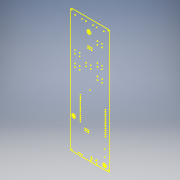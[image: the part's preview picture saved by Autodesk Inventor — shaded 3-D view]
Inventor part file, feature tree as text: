
AUTODESK INVENTOR PART (.ipt)
format: ipt  version: 2019 (Build 230136000, 136)  size: 111,616 bytes
history: native  units: mm
features: other x3, sketch x1, reference x1
ambient origin geometry x8: Origin, YZ Plane, XZ Plane, XY Plane, X Axis, Y Axis, Z Axis, Center Point
feature tree (5):
  sketch  "Skizze1"
  reference  "Referenz1"
  other  "Baugruppe1"
  other  "fantimote.kicad_pcb:1"
  other  "fantimote.kicad_pcb_Kontur:1"
